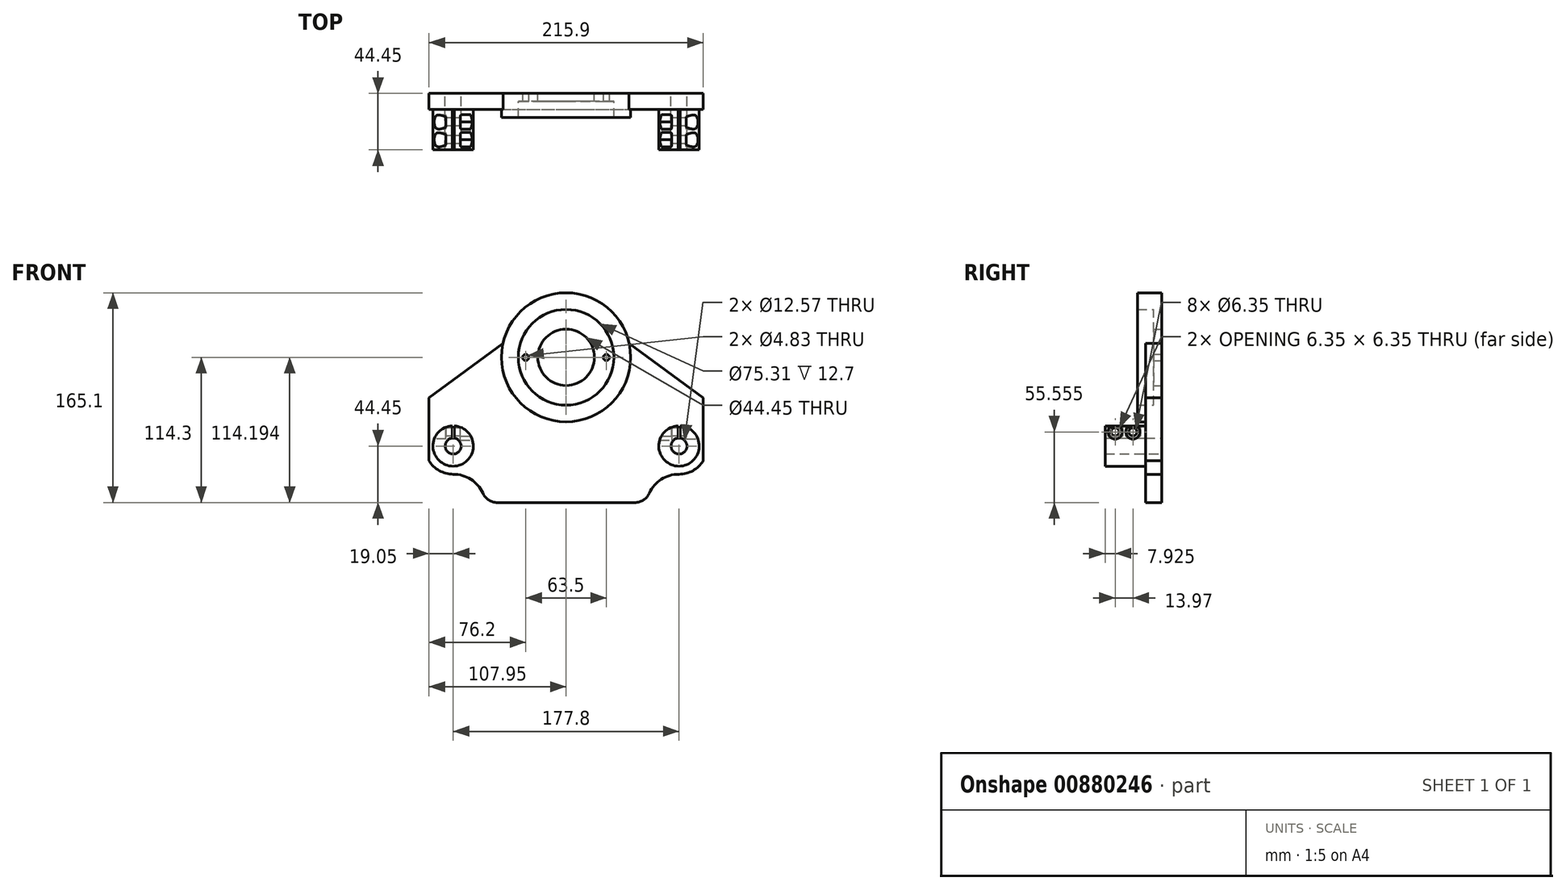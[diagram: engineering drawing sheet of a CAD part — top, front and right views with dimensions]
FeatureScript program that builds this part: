
annotation { "Feature Type Name" : "Feature", "Feature Type Description" : "" }
export const myFeature = defineFeature(function(context is Context, id is Id, definition is map)
    precondition{}
    {
        {
            var Q0;
            Q0=qCreatedBy(makeId("Front.planeOp"),FACE);
            var sketch = newSketch(context, id + "F0", { "sketchPlane" : qUnion([Q0])});
            skCircle(sketch, "E0", {"center": v(-88.9, 0) * mm, "radius": 6.29 * mm});
            skCircle(sketch, "E1", {"center": v(88.9, 0) * mm, "radius": 6.29 * mm});
            skCircle(sketch, "E2", {"center": v(-88.9, -44.45) * mm, "radius": 4.76 * mm});
            skCircle(sketch, "E3", {"center": v(88.9, -44.45) * mm, "radius": 4.76 * mm});
            skLineSegment(sketch, "E4.top", {"start": v(-107.95, -69.85) * mm, "end": v(107.95, -69.85) * mm});
            skLineSegment(sketch, "E4.left", {"start": v(-107.95, 38.1) * mm, "end": v(-107.95, -69.85) * mm});
            skLineSegment(sketch, "E4.right", {"start": v(107.95, 38.1) * mm, "end": v(107.95, -69.85) * mm});
            skPoint(sketch, "E4.middle", {"position": v(0, -15.87) * mm});
            skCircle(sketch, "E5", {"center": v(0, 69.85) * mm, "radius": 37.66 * mm});
            skArc(sketch, "E6", {"start": v(22.5, 100.6) * mm, "mid": v(0, 107.95) * mm, "end": v(-22.5, 100.6) * mm});
            skLineSegment(sketch, "E7", {"start": v(-107.95, 38.1) * mm, "end": v(-22.5, 100.6) * mm});
            skLineSegment(sketch, "E8", {"start": v(107.95, 38.1) * mm, "end": v(22.5, 100.6) * mm});
            skPoint(sketch, "E9.center.orphan", {"position": v(0, 0) * mm});
            skSolve(sketch);
        }
        {
            var Q0;
            Q0=qSketchRegion(id+"F0",true);
            extrude(context, id + "F1", {"entities" : qUnion([Q0]), "depth" : 12.7 * mm});
        }
        {
            var Q0;
            Q0=makeQuery(id+"F1.opExtrude","CAP_FACE",FACE,{"disambiguationData":[OSD([sQuery(id+"F0.wireOp",EDGE,"E9"),sQuery(id+"F0.wireOp",EDGE,"E0"),sQuery(id+"F0.wireOp",EDGE,"E1"),sQuery(id+"F0.wireOp",EDGE,"E2"),sQuery(id+"F0.wireOp",EDGE,"E3"),sQuery(id+"F0.wireOp",EDGE,"E4.bottom"),sQuery(id+"F0.wireOp",EDGE,"E4.top"),sQuery(id+"F0.wireOp",EDGE,"E4.left"),sQuery(id+"F0.wireOp",EDGE,"E4.right")])],"isStart":false});
            var sketch = newSketch(context, id + "F2", { "sketchPlane" : qUnion([Q0])});
            skCircle(sketch, "E10", {"center": v(0, -107.95) * mm, "radius": 63.5 * mm});
            skSolve(sketch);
        }
        {
            var Q0;
            Q0=qSketchRegion(id+"F2",true);
            extrude(context, id + "F3", {"entities" : qUnion([Q0]), "operationType" : NewBodyOperationType.REMOVE, "oppositeDirection" : true, "depth" : 25.4 * mm});
        }
        {
            var Q0;
            Q0=makeQuery(id+"F3.boolean.opBoolean","INTERSECT",EDGE,{"disambiguationData":[OD(0.0)],"derivedFrom":[makeQuery(id+"F1.opExtrude","SWEPT_FACE",FACE,{"disambiguationData":[OSD([sQuery(id+"F0.wireOp",EDGE,"E4.top")])]}),makeQuery(id+"F3.opExtrude","SWEPT_FACE",FACE,{"disambiguationData":[OSD([sQuery(id+"F2.wireOp",EDGE,"E10")])]})]});
            var Q1;
            Q1=makeQuery(id+"F3.boolean.opBoolean","INTERSECT",EDGE,{"disambiguationData":[OD(1.0)],"derivedFrom":[makeQuery(id+"F1.opExtrude","SWEPT_FACE",FACE,{"disambiguationData":[OSD([sQuery(id+"F0.wireOp",EDGE,"E4.top")])]}),makeQuery(id+"F3.opExtrude","SWEPT_FACE",FACE,{"disambiguationData":[OSD([sQuery(id+"F2.wireOp",EDGE,"E10")])]})]});
            fillet(context, id + "F4", {"entities" : qUnion([Q0, Q1]), "radius" : 12.7 * mm, "tangentPropagation" : true, "allowEdgeOverflow" : false});
        }
        {
            var Q0;
            Q0=makeQuery(id+"F1.opExtrude","CAP_FACE",FACE,{"disambiguationData":[OSD([sQuery(id+"F0.wireOp",EDGE,"E9"),sQuery(id+"F0.wireOp",EDGE,"E0"),sQuery(id+"F0.wireOp",EDGE,"E1"),sQuery(id+"F0.wireOp",EDGE,"E2"),sQuery(id+"F0.wireOp",EDGE,"E3"),sQuery(id+"F0.wireOp",EDGE,"E4.bottom"),sQuery(id+"F0.wireOp",EDGE,"E4.top"),sQuery(id+"F0.wireOp",EDGE,"E4.left"),sQuery(id+"F0.wireOp",EDGE,"E4.right")])],"isStart":false});
            var sketch = newSketch(context, id + "F5", { "sketchPlane" : qUnion([Q0])});
            skCircle(sketch, "E11.0", {"center": v(-88.9, 0) * mm, "radius": 6.29 * mm});
            skCircle(sketch, "E12", {"center": v(-88.9, 0) * mm, "radius": 15.88 * mm});
            skCircle(sketch, "E13.0", {"center": v(88.9, 0) * mm, "radius": 6.29 * mm});
            skCircle(sketch, "E14", {"center": v(88.9, 0) * mm, "radius": 15.88 * mm});
            skSolve(sketch);
        }
        {
            var Q0;
            Q0=qSketchRegion(id+"F5",true);
            extrude(context, id + "F6", {"entities" : qUnion([Q0]), "operationType" : NewBodyOperationType.ADD, "depth" : 31.75 * mm});
        }
        {
            var Q0;
            Q0=makeQuery(id+"F6.opExtrude","CAP_FACE",FACE,{"disambiguationData":[OSD([sQuery(id+"F5.wireOp",EDGE,"E11.0"),sQuery(id+"F5.wireOp",EDGE,"E12")])],"isStart":false});
            var sketch = newSketch(context, id + "F7", { "sketchPlane" : qUnion([Q0])});
            skLineSegment(sketch, "E15.bottom", {"start": v(-89.7, 1.72) * mm, "end": v(-88.1, 1.72) * mm});
            skLineSegment(sketch, "E15.top", {"start": v(-89.7, 19.66) * mm, "end": v(-88.1, 19.66) * mm});
            skLineSegment(sketch, "E15.left", {"start": v(-89.7, 1.72) * mm, "end": v(-89.7, 19.66) * mm});
            skLineSegment(sketch, "E15.right", {"start": v(-88.1, 1.72) * mm, "end": v(-88.1, 19.66) * mm});
            skLineSegment(sketch, "E16", {"start": v(-88.9, 1.72) * mm, "end": v(-88.9, 0) * mm});
            skPoint(sketch, "E16.endSnap0", {"position": v(-88.9, 1.72) * mm});
            skLineSegment(sketch, "E17.bottom", {"start": v(88.1, 20.83) * mm, "end": v(89.7, 20.83) * mm});
            skLineSegment(sketch, "E17.top", {"start": v(88.1, 3.08) * mm, "end": v(89.7, 3.08) * mm});
            skLineSegment(sketch, "E17.left", {"start": v(88.1, 20.83) * mm, "end": v(88.1, 3.08) * mm});
            skLineSegment(sketch, "E17.right", {"start": v(89.7, 20.83) * mm, "end": v(89.7, 3.08) * mm});
            skLineSegment(sketch, "E18", {"start": v(88.9, 0) * mm, "end": v(88.9, 3.08) * mm});
            skSolve(sketch);
        }
        {
            var Q0;
            Q0=qSketchRegion(id+"F7",true);
            var Q1;
            Q1=makeQuery(id+"F1.opExtrude","CAP_FACE",FACE,{"disambiguationData":[OSD([sQuery(id+"F0.wireOp",EDGE,"E9"),sQuery(id+"F0.wireOp",EDGE,"E0"),sQuery(id+"F0.wireOp",EDGE,"E1"),sQuery(id+"F0.wireOp",EDGE,"E2"),sQuery(id+"F0.wireOp",EDGE,"E3"),sQuery(id+"F0.wireOp",EDGE,"E4.bottom"),sQuery(id+"F0.wireOp",EDGE,"E4.top"),sQuery(id+"F0.wireOp",EDGE,"E4.left"),sQuery(id+"F0.wireOp",EDGE,"E4.right")])],"isStart":false});
            extrude(context, id + "F8", {"entities" : qUnion([Q0]), "operationType" : NewBodyOperationType.REMOVE, "endBound" : BoundingType.UP_TO_SURFACE, "oppositeDirection" : true, "endBoundEntityFace" : qUnion([Q1]), "depth" : 25.4 * mm});
        }
        {
            var Q0;
            Q0=makeQuery(id+"F1.opExtrude","SWEPT_FACE",FACE,{"disambiguationData":[OSD([sQuery(id+"F0.wireOp",EDGE,"E4.left")])]});
            var sketch = newSketch(context, id + "F9", { "sketchPlane" : qUnion([Q0])});
            skCircle(sketch, "E19", {"center": v(36.53, 11.1) * mm, "radius": 3.18 * mm});
            skCircle(sketch, "E20", {"center": v(22.56, 11.1) * mm, "radius": 3.18 * mm});
            skSolve(sketch);
        }
        {
            var Q0;
            Q0=qSketchRegion(id+"F9",true);
            extrude(context, id + "F10", {"entities" : qUnion([Q0]), "operationType" : NewBodyOperationType.REMOVE, "oppositeDirection" : true, "depth" : 224.54 * mm});
        }
        {
            var Q0;
            Q0=qCreatedBy(makeId("Right.planeOp"),FACE);
            var sketch = newSketch(context, id + "F11", { "sketchPlane" : qUnion([Q0])});
            skCircle(sketch, "E21.0", {"center": v(-36.53, 11.1) * mm, "radius": 3.17 * mm, "construction": true});
            skCircle(sketch, "E22.0", {"center": v(-22.56, 11.1) * mm, "radius": 3.18 * mm, "construction": true});
            skCircle(sketch, "E23.cCircle", {"center": v(-36.53, 11.1) * mm, "radius": 6.6 * mm, "construction": true});
            skLineSegment(sketch, "E23.0", {"start": v(-36.53, 17.7) * mm, "end": v(-30.8, 14.4) * mm});
            skLineSegment(sketch, "E23.1", {"start": v(-30.8, 14.4) * mm, "end": v(-30.8, 7.8) * mm});
            skLineSegment(sketch, "E23.2", {"start": v(-30.8, 7.8) * mm, "end": v(-36.53, 4.5) * mm});
            skLineSegment(sketch, "E23.3", {"start": v(-36.53, 4.5) * mm, "end": v(-42.24, 7.8) * mm});
            skLineSegment(sketch, "E23.4", {"start": v(-42.24, 7.8) * mm, "end": v(-42.24, 14.4) * mm});
            skLineSegment(sketch, "E23.5", {"start": v(-42.24, 14.4) * mm, "end": v(-36.53, 17.7) * mm});
            skCircle(sketch, "E24.cCircle", {"center": v(-22.56, 11.1) * mm, "radius": 6.6 * mm, "construction": true});
            skLineSegment(sketch, "E24.0", {"start": v(-28.27, 14.4) * mm, "end": v(-22.56, 17.7) * mm});
            skLineSegment(sketch, "E24.1", {"start": v(-22.56, 17.7) * mm, "end": v(-16.84, 14.4) * mm});
            skLineSegment(sketch, "E24.2", {"start": v(-16.84, 14.4) * mm, "end": v(-16.84, 7.8) * mm});
            skLineSegment(sketch, "E24.3", {"start": v(-16.84, 7.8) * mm, "end": v(-22.56, 4.5) * mm});
            skLineSegment(sketch, "E24.4", {"start": v(-22.56, 4.5) * mm, "end": v(-28.27, 7.8) * mm});
            skLineSegment(sketch, "E24.5", {"start": v(-28.27, 7.8) * mm, "end": v(-28.27, 14.4) * mm});
            skSolve(sketch);
        }
        {
            var Q0;
            Q0=makeQuery(id+"F11.imprint","IMPRINT",FACE,{"disambiguationData":[TD([[makeQuery(id+"F11.imprint","IMPRINT",EDGE,{"derivedFrom":sQuery(id+"F11.wireOp",EDGE,"E23.0")}),-1.0]])]});
            var Q1;
            Q1=makeQuery(id+"F11.imprint","IMPRINT",FACE,{"disambiguationData":[TD([[makeQuery(id+"F11.imprint","IMPRINT",EDGE,{"derivedFrom":sQuery(id+"F11.wireOp",EDGE,"E24.0")}),-1.0]])]});
            var Q2;
            Q2=sQuery(id+"F11.wireOp",EDGE,"E21.0");
            var Q3;
            Q3=sQuery(id+"F11.wireOp",EDGE,"E22.0");
            extrude(context, id + "F12", {"entities" : qUnion([Q0, Q1]), "operationType" : NewBodyOperationType.REMOVE, "surfaceEntities" : qUnion([Q2, Q3]), "oppositeDirection" : true, "depth" : 83.18 * mm, "hasSecondDirection" : true, "secondDirectionOppositeDirection" : false, "secondDirectionDepth" : 83.18 * mm});
        }
        {
            var Q0;
            Q0=makeQuery(id+"F1.opExtrude","SWEPT_FACE",FACE,{"disambiguationData":[OSD([sQuery(id+"F0.wireOp",EDGE,"E4.left")])]});
            var sketch = newSketch(context, id + "F13", { "sketchPlane" : qUnion([Q0])});
            skCircle(sketch, "E25.0", {"center": v(36.53, 11.1) * mm, "radius": 3.17 * mm, "construction": true});
            skCircle(sketch, "E26.0", {"center": v(22.56, 11.1) * mm, "radius": 3.18 * mm, "construction": true});
            skCircle(sketch, "E27", {"center": v(22.56, 11.1) * mm, "radius": 5.56 * mm});
            skCircle(sketch, "E28", {"center": v(36.53, 11.1) * mm, "radius": 5.56 * mm});
            skSolve(sketch);
        }
        {
            var Q0;
            Q0=qSketchRegion(id+"F13",true);
            extrude(context, id + "F14", {"entities" : qUnion([Q0]), "operationType" : NewBodyOperationType.REMOVE, "oppositeDirection" : true, "depth" : 13.33 * mm});
        }
        {
            var Q0;
            Q0=makeQuery(id+"F1.opExtrude","SWEPT_FACE",FACE,{"disambiguationData":[OSD([sQuery(id+"F0.wireOp",EDGE,"E4.right")])]});
            var sketch = newSketch(context, id + "F15", { "sketchPlane" : qUnion([Q0])});
            skCircle(sketch, "E29.0", {"center": v(-36.53, 11.1) * mm, "radius": 3.17 * mm, "construction": true});
            skCircle(sketch, "E29.1", {"center": v(-22.56, 11.1) * mm, "radius": 3.18 * mm, "construction": true});
            skCircle(sketch, "E30", {"center": v(-36.53, 11.1) * mm, "radius": 5.56 * mm});
            skCircle(sketch, "E31", {"center": v(-22.56, 11.1) * mm, "radius": 5.56 * mm});
            skSolve(sketch);
        }
        {
            var Q0;
            Q0=qSketchRegion(id+"F15",true);
            extrude(context, id + "F16", {"entities" : qUnion([Q0]), "operationType" : NewBodyOperationType.REMOVE, "oppositeDirection" : true, "depth" : 13.33 * mm});
        }
        {
            var Q0;
            {var subQ1=sQuery(id+"F0.wireOp",EDGE,"E4.left");var subQ2=sQuery(id+"F0.wireOp",EDGE,"E4.top");Q0=makeQuery(id+"F3.boolean.opBoolean","SPLIT",FACE,{"disambiguationData":[TD([makeQuery(id+"F1.opExtrude","SWEPT_FACE",FACE,{"disambiguationData":[OSD([subQ1])]})])],"derivedFrom":makeQuery(id+"F1.opExtrude","SWEPT_FACE",FACE,{"disambiguationData":[OSD([subQ2])]})});}
            var sketch = newSketch(context, id + "F17", { "sketchPlane" : qUnion([Q0])});
            skLineSegment(sketch, "E32.0", {"start": v(56.8, 12.7) * mm, "end": v(107.95, 12.7) * mm});
            skLineSegment(sketch, "E33", {"start": v(107.95, 12.7) * mm, "end": v(107.95, 31.75) * mm});
            skLineSegment(sketch, "E34", {"start": v(107.95, 31.75) * mm, "end": v(56.8, 31.75) * mm});
            skLineSegment(sketch, "E35", {"start": v(56.8, 31.75) * mm, "end": v(56.8, 12.7) * mm});
            skCircle(sketch, "E36", {"center": v(82.37, 22.23) * mm, "radius": 3.18 * mm});
            skLineSegment(sketch, "E37", {"start": v(107.95, 22.23) * mm, "end": v(56.8, 22.23) * mm, "construction": true});
            skLineSegment(sketch, "E38.bottom", {"start": v(-107.95, 12.7) * mm, "end": v(-56.8, 12.7) * mm});
            skLineSegment(sketch, "E38.top", {"start": v(-107.95, 31.75) * mm, "end": v(-56.8, 31.75) * mm});
            skLineSegment(sketch, "E38.left", {"start": v(-107.95, 12.7) * mm, "end": v(-107.95, 31.75) * mm});
            skLineSegment(sketch, "E38.right", {"start": v(-56.8, 12.7) * mm, "end": v(-56.8, 31.75) * mm});
            skCircle(sketch, "E39", {"center": v(-82.37, 22.22) * mm, "radius": 3.18 * mm});
            skPoint(sketch, "E39.centerSnap0", {"position": v(-82.37, 31.75) * mm});
            skSolve(sketch);
        }
        {
            var Q0;
            Q0=qSketchRegion(id+"F17",true);
            extrude(context, id + "F18", {"entities" : qUnion([Q0]), "operationType" : NewBodyOperationType.ADD, "oppositeDirection" : true, "depth" : 4.75 * mm});
        }
        {
            var Q0;
            Q0=makeQuery(id+"F18.opExtrude","SWEPT_EDGE",EDGE,{"disambiguationData":[OSD([sQuery(id+"F17.wireOp",EDGE,"E34"),sQuery(id+"F17.wireOp",EDGE,"E35")])]});
            var Q1;
            Q1=makeQuery(id+"F18.opExtrude","SWEPT_EDGE",EDGE,{"disambiguationData":[OSD([sQuery(id+"F17.wireOp",EDGE,"E33"),sQuery(id+"F17.wireOp",EDGE,"E34")])]});
            var Q2;
            Q2=makeQuery(id+"F18.opExtrude","SWEPT_EDGE",EDGE,{"disambiguationData":[OSD([sQuery(id+"F17.wireOp",EDGE,"E38.top"),sQuery(id+"F17.wireOp",EDGE,"E38.right")])]});
            var Q3;
            Q3=makeQuery(id+"F18.opExtrude","SWEPT_EDGE",EDGE,{"disambiguationData":[OSD([sQuery(id+"F17.wireOp",EDGE,"E38.top"),sQuery(id+"F17.wireOp",EDGE,"E38.left")])]});
            fillet(context, id + "F19", {"entities" : qUnion([Q0, Q1, Q2, Q3]), "radius" : 12.7 * mm, "tangentPropagation" : true, "allowEdgeOverflow" : false});
        }
        {
            var Q0;
            {var subQ0=sQuery(id+"F0.wireOp",EDGE,"E8");var subQ1=sQuery(id+"F0.wireOp",EDGE,"E7");var subQ2=sQuery(id+"F0.wireOp",EDGE,"E6");var subQ3=sQuery(id+"F0.wireOp",EDGE,"E5");var subQ4=sQuery(id+"F0.wireOp",EDGE,"E4.right");var subQ5=sQuery(id+"F0.wireOp",EDGE,"E4.left");var subQ6=sQuery(id+"F0.wireOp",EDGE,"E4.top");var subQ7=sQuery(id+"F0.wireOp",EDGE,"E3");var subQ8=sQuery(id+"F0.wireOp",EDGE,"E2");var subQ9=sQuery(id+"F0.wireOp",EDGE,"E1");var subQ10=sQuery(id+"F0.wireOp",EDGE,"E0");var subQ11=sQuery(id+"F7.wireOp",EDGE,"E15.bottom");Q0=makeQuery(id+"F8.boolean.opBoolean","MERGE",FACE,{"derivedFrom":[makeQuery(id+"F1.opExtrude","CAP_FACE",FACE,{"disambiguationData":[OSD([subQ10,subQ9,subQ8,subQ7,subQ6,subQ5,subQ4,subQ3,subQ2,subQ1,subQ0])],"isStart":false}),makeQuery(id+"F8.opExtrude","CAP_FACE",FACE,{"disambiguationData":[OSD([subQ10,subQ9,subQ8,subQ7,subQ6,subQ5,subQ4,subQ3,subQ2,subQ1,subQ0]),ownerDisambiguation([makeQuery(id+"F7.imprint","IMPRINT",EDGE,{"disambiguationData":[TD([[makeQuery(id+"F7.imprint","IMPRINT",VERTEX,{"derivedFrom":subQ11}),1.0]])],"derivedFrom":subQ11})])],"isStart":false}),makeQuery(id+"F8.opExtrude","CAP_FACE",FACE,{"disambiguationData":[OSD([subQ10,subQ9,subQ8,subQ7,subQ6,subQ5,subQ4,subQ3,subQ2,subQ1,subQ0]),ownerDisambiguation([makeQuery(id+"F7.imprint","IMPRINT",EDGE,{"derivedFrom":sQuery(id+"F7.wireOp",EDGE,"E17.bottom")})])],"isStart":false})]});}
            var sketch = newSketch(context, id + "F20", { "sketchPlane" : qUnion([Q0])});
            skCircle(sketch, "E40", {"center": v(0, 69.85) * mm, "radius": 50.8 * mm});
            skCircle(sketch, "E41.0", {"center": v(0, 69.85) * mm, "radius": 37.66 * mm});
            skSolve(sketch);
        }
        {
            var Q0;
            Q0=qSketchRegion(id+"F20",true);
            extrude(context, id + "F21", {"entities" : qUnion([Q0]), "operationType" : NewBodyOperationType.ADD, "oppositeDirection" : true, "depth" : 12.7 * mm});
        }
        {
            var Q0;
            Q0=makeQuery(id+"F21.boolean.opBoolean","MERGE",FACE,{"derivedFrom":[makeQuery(id+"F1.opExtrude","CAP_FACE",FACE,{"disambiguationData":[OSD([sQuery(id+"F0.wireOp",EDGE,"E0"),sQuery(id+"F0.wireOp",EDGE,"E1"),sQuery(id+"F0.wireOp",EDGE,"E2"),sQuery(id+"F0.wireOp",EDGE,"E3"),sQuery(id+"F0.wireOp",EDGE,"E4.top"),sQuery(id+"F0.wireOp",EDGE,"E4.left"),sQuery(id+"F0.wireOp",EDGE,"E4.right"),sQuery(id+"F0.wireOp",EDGE,"E5"),sQuery(id+"F0.wireOp",EDGE,"E6"),sQuery(id+"F0.wireOp",EDGE,"E7"),sQuery(id+"F0.wireOp",EDGE,"E8")])],"isStart":true}),makeQuery(id+"F21.opExtrude","CAP_FACE",FACE,{"disambiguationData":[OSD([sQuery(id+"F20.wireOp",EDGE,"E40"),sQuery(id+"F20.wireOp",EDGE,"E41.0")])],"isStart":false})]});
            var sketch = newSketch(context, id + "F22", { "sketchPlane" : qUnion([Q0])});
            skCircle(sketch, "E42.0", {"center": v(0, 69.85) * mm, "radius": 37.66 * mm});
            skCircle(sketch, "E43", {"center": v(0, 69.85) * mm, "radius": 22.23 * mm});
            skSolve(sketch);
        }
        {
            var Q0;
            Q0=qSketchRegion(id+"F22",true);
            extrude(context, id + "F23", {"entities" : qUnion([Q0]), "operationType" : NewBodyOperationType.ADD, "oppositeDirection" : true, "depth" : 6.35 * mm});
        }
        {
            var Q0;
            Q0=makeQuery(id+"F23.boolean.opBoolean","MERGE",FACE,{"derivedFrom":[makeQuery(id+"F21.boolean.opBoolean","MERGE",FACE,{"derivedFrom":[makeQuery(id+"F1.opExtrude","CAP_FACE",FACE,{"disambiguationData":[OSD([sQuery(id+"F0.wireOp",EDGE,"E0"),sQuery(id+"F0.wireOp",EDGE,"E1"),sQuery(id+"F0.wireOp",EDGE,"E2"),sQuery(id+"F0.wireOp",EDGE,"E3"),sQuery(id+"F0.wireOp",EDGE,"E4.top"),sQuery(id+"F0.wireOp",EDGE,"E4.left"),sQuery(id+"F0.wireOp",EDGE,"E4.right"),sQuery(id+"F0.wireOp",EDGE,"E5"),sQuery(id+"F0.wireOp",EDGE,"E6"),sQuery(id+"F0.wireOp",EDGE,"E7"),sQuery(id+"F0.wireOp",EDGE,"E8")])],"isStart":true}),makeQuery(id+"F21.opExtrude","CAP_FACE",FACE,{"disambiguationData":[OSD([sQuery(id+"F20.wireOp",EDGE,"E40"),sQuery(id+"F20.wireOp",EDGE,"E41.0")])],"isStart":false})]}),makeQuery(id+"F23.opExtrude","CAP_FACE",FACE,{"disambiguationData":[OSD([sQuery(id+"F22.wireOp",EDGE,"E42.0"),sQuery(id+"F22.wireOp",EDGE,"E43")])],"isStart":true})]});
            var sketch = newSketch(context, id + "F24", { "sketchPlane" : qUnion([Q0])});
            skCircle(sketch, "E44", {"center": v(-31.75, 69.74) * mm, "radius": 2.41 * mm});
            skCircle(sketch, "E45", {"center": v(31.75, 69.74) * mm, "radius": 2.41 * mm});
            skLineSegment(sketch, "E46", {"start": v(-31.75, 69.74) * mm, "end": v(0, 69.74) * mm, "construction": true});
            skLineSegment(sketch, "E47", {"start": v(0, 69.74) * mm, "end": v(31.75, 69.74) * mm, "construction": true});
            skSolve(sketch);
        }
        {
            var Q0;
            Q0=qSketchRegion(id+"F24",true);
            extrude(context, id + "F25", {"entities" : qUnion([Q0]), "operationType" : NewBodyOperationType.REMOVE, "oppositeDirection" : true, "depth" : 25.4 * mm});
        }
        {
            var Q0;
            {var subQ0=sQuery(id+"F0.wireOp",EDGE,"E8");var subQ1=sQuery(id+"F0.wireOp",EDGE,"E7");var subQ2=sQuery(id+"F0.wireOp",EDGE,"E6");var subQ3=sQuery(id+"F0.wireOp",EDGE,"E5");var subQ4=sQuery(id+"F0.wireOp",EDGE,"E4.right");var subQ5=sQuery(id+"F0.wireOp",EDGE,"E4.left");var subQ6=sQuery(id+"F0.wireOp",EDGE,"E4.top");var subQ7=sQuery(id+"F0.wireOp",EDGE,"E3");var subQ8=sQuery(id+"F0.wireOp",EDGE,"E2");var subQ9=sQuery(id+"F0.wireOp",EDGE,"E1");var subQ10=sQuery(id+"F0.wireOp",EDGE,"E0");var subQ11=sQuery(id+"F7.wireOp",EDGE,"E15.bottom");Q0=makeQuery(id+"F21.boolean.opBoolean","MERGE",FACE,{"derivedFrom":[makeQuery(id+"F8.boolean.opBoolean","MERGE",FACE,{"derivedFrom":[makeQuery(id+"F1.opExtrude","CAP_FACE",FACE,{"disambiguationData":[OSD([subQ10,subQ9,subQ8,subQ7,subQ6,subQ5,subQ4,subQ3,subQ2,subQ1,subQ0])],"isStart":false}),makeQuery(id+"F8.opExtrude","CAP_FACE",FACE,{"disambiguationData":[OSD([subQ10,subQ9,subQ8,subQ7,subQ6,subQ5,subQ4,subQ3,subQ2,subQ1,subQ0]),ownerDisambiguation([makeQuery(id+"F7.imprint","IMPRINT",EDGE,{"disambiguationData":[TD([[makeQuery(id+"F7.imprint","IMPRINT",VERTEX,{"derivedFrom":subQ11}),1.0]])],"derivedFrom":subQ11})])],"isStart":false}),makeQuery(id+"F8.opExtrude","CAP_FACE",FACE,{"disambiguationData":[OSD([subQ10,subQ9,subQ8,subQ7,subQ6,subQ5,subQ4,subQ3,subQ2,subQ1,subQ0]),ownerDisambiguation([makeQuery(id+"F7.imprint","IMPRINT",EDGE,{"derivedFrom":sQuery(id+"F7.wireOp",EDGE,"E17.bottom")})])],"isStart":false})]}),makeQuery(id+"F21.opExtrude","CAP_FACE",FACE,{"disambiguationData":[OSD([sQuery(id+"F20.wireOp",EDGE,"E40"),sQuery(id+"F20.wireOp",EDGE,"E41.0")])],"isStart":true})]});}
            var sketch = newSketch(context, id + "F26", { "sketchPlane" : qUnion([Q0])});
            skCircle(sketch, "E48.0", {"center": v(0, 69.85) * mm, "radius": 37.66 * mm});
            skCircle(sketch, "E49", {"center": v(0, 69.85) * mm, "radius": 50.8 * mm});
            skSolve(sketch);
        }
        {
            var Q0;
            Q0=qSketchRegion(id+"F26",true);
            extrude(context, id + "F27", {"entities" : qUnion([Q0]), "operationType" : NewBodyOperationType.ADD, "depth" : 6.35 * mm});
        }
        {
            var Q0;
            {var subQ0=sQuery(id+"F0.wireOp",EDGE,"E8");var subQ1=sQuery(id+"F0.wireOp",EDGE,"E7");var subQ2=sQuery(id+"F0.wireOp",EDGE,"E6");var subQ3=sQuery(id+"F0.wireOp",EDGE,"E5");var subQ4=sQuery(id+"F0.wireOp",EDGE,"E4.right");var subQ5=sQuery(id+"F0.wireOp",EDGE,"E4.left");var subQ6=sQuery(id+"F0.wireOp",EDGE,"E4.top");var subQ7=sQuery(id+"F0.wireOp",EDGE,"E3");var subQ8=sQuery(id+"F0.wireOp",EDGE,"E2");var subQ9=sQuery(id+"F0.wireOp",EDGE,"E1");var subQ10=sQuery(id+"F0.wireOp",EDGE,"E0");var subQ11=sQuery(id+"F7.wireOp",EDGE,"E15.bottom");Q0=makeQuery(id+"F21.boolean.opBoolean","MERGE",FACE,{"derivedFrom":[makeQuery(id+"F8.boolean.opBoolean","MERGE",FACE,{"derivedFrom":[makeQuery(id+"F1.opExtrude","CAP_FACE",FACE,{"disambiguationData":[OSD([subQ10,subQ9,subQ8,subQ7,subQ6,subQ5,subQ4,subQ3,subQ2,subQ1,subQ0])],"isStart":false}),makeQuery(id+"F8.opExtrude","CAP_FACE",FACE,{"disambiguationData":[OSD([subQ10,subQ9,subQ8,subQ7,subQ6,subQ5,subQ4,subQ3,subQ2,subQ1,subQ0]),ownerDisambiguation([makeQuery(id+"F7.imprint","IMPRINT",EDGE,{"disambiguationData":[TD([[makeQuery(id+"F7.imprint","IMPRINT",VERTEX,{"derivedFrom":subQ11}),1.0]])],"derivedFrom":subQ11})])],"isStart":false}),makeQuery(id+"F8.opExtrude","CAP_FACE",FACE,{"disambiguationData":[OSD([subQ10,subQ9,subQ8,subQ7,subQ6,subQ5,subQ4,subQ3,subQ2,subQ1,subQ0]),ownerDisambiguation([makeQuery(id+"F7.imprint","IMPRINT",EDGE,{"derivedFrom":sQuery(id+"F7.wireOp",EDGE,"E17.bottom")})])],"isStart":false})]}),makeQuery(id+"F21.opExtrude","CAP_FACE",FACE,{"disambiguationData":[OSD([sQuery(id+"F20.wireOp",EDGE,"E40"),sQuery(id+"F20.wireOp",EDGE,"E41.0")])],"isStart":true})]});}
            var sketch = newSketch(context, id + "F28", { "sketchPlane" : qUnion([Q0])});
            skArc(sketch, "E50", {"start": v(-111.1, 1.11) * mm, "mid": v(-92.44, -21.94) * mm, "end": v(-67.48, -5.93) * mm});
            skArc(sketch, "E51", {"start": v(67.48, -5.93) * mm, "mid": v(92.52, -21.93) * mm, "end": v(111.09, 1.27) * mm});
            skLineSegment(sketch, "E52", {"start": v(-43, 12.7) * mm, "end": v(43, 12.7) * mm});
            skLineSegment(sketch, "E53", {"start": v(-111.1, 1.11) * mm, "end": v(-111.1, -81.42) * mm});
            skLineSegment(sketch, "E54", {"start": v(-111.1, -81.42) * mm, "end": v(111.09, -81.42) * mm});
            skLineSegment(sketch, "E55", {"start": v(111.09, -81.42) * mm, "end": v(111.09, 1.27) * mm});
            skLineSegment(sketch, "E56", {"start": v(0, 12.7) * mm, "end": v(0, 0) * mm, "construction": true});
            skPoint(sketch, "E57.newPointB", {"position": v(38.1, 12.7) * mm});
            skArc(sketch, "E57.filletArc", {"start": v(67.48, -5.93) * mm, "mid": v(58.38, 7.51) * mm, "end": v(43, 12.7) * mm});
            skPoint(sketch, "E58.newPointB", {"position": v(-38.1, 12.7) * mm});
            skArc(sketch, "E58.filletArc", {"start": v(-43, 12.7) * mm, "mid": v(-58.38, 7.51) * mm, "end": v(-67.48, -5.93) * mm});
            skSolve(sketch);
        }
        {
            var Q0;
            Q0=qSketchRegion(id+"F28",true);
            extrude(context, id + "F29", {"entities" : qUnion([Q0]), "operationType" : NewBodyOperationType.REMOVE, "oppositeDirection" : true, "depth" : 25.4 * mm, "hasSecondDirection" : true, "secondDirectionOppositeDirection" : false, "secondDirectionDepth" : 25.4 * mm});
        }
        {
            var Q0;
            {var subQ0=sQuery(id+"F0.wireOp",EDGE,"E8");var subQ1=sQuery(id+"F0.wireOp",EDGE,"E7");var subQ2=sQuery(id+"F0.wireOp",EDGE,"E6");var subQ3=sQuery(id+"F0.wireOp",EDGE,"E5");var subQ4=sQuery(id+"F0.wireOp",EDGE,"E4.right");var subQ5=sQuery(id+"F0.wireOp",EDGE,"E4.left");var subQ6=sQuery(id+"F0.wireOp",EDGE,"E4.top");var subQ7=sQuery(id+"F0.wireOp",EDGE,"E3");var subQ8=sQuery(id+"F0.wireOp",EDGE,"E2");var subQ9=sQuery(id+"F0.wireOp",EDGE,"E1");var subQ10=sQuery(id+"F0.wireOp",EDGE,"E0");var subQ11=sQuery(id+"F7.wireOp",EDGE,"E15.bottom");Q0=makeQuery(id+"F21.boolean.opBoolean","MERGE",FACE,{"derivedFrom":[makeQuery(id+"F8.boolean.opBoolean","MERGE",FACE,{"derivedFrom":[makeQuery(id+"F1.opExtrude","CAP_FACE",FACE,{"disambiguationData":[OSD([subQ10,subQ9,subQ8,subQ7,subQ6,subQ5,subQ4,subQ3,subQ2,subQ1,subQ0])],"isStart":false}),makeQuery(id+"F8.opExtrude","CAP_FACE",FACE,{"disambiguationData":[OSD([subQ10,subQ9,subQ8,subQ7,subQ6,subQ5,subQ4,subQ3,subQ2,subQ1,subQ0]),ownerDisambiguation([makeQuery(id+"F7.imprint","IMPRINT",EDGE,{"disambiguationData":[TD([[makeQuery(id+"F7.imprint","IMPRINT",VERTEX,{"derivedFrom":subQ11}),1.0]])],"derivedFrom":subQ11})])],"isStart":false}),makeQuery(id+"F8.opExtrude","CAP_FACE",FACE,{"disambiguationData":[OSD([subQ10,subQ9,subQ8,subQ7,subQ6,subQ5,subQ4,subQ3,subQ2,subQ1,subQ0]),ownerDisambiguation([makeQuery(id+"F7.imprint","IMPRINT",EDGE,{"derivedFrom":sQuery(id+"F7.wireOp",EDGE,"E17.bottom")})])],"isStart":false})]}),makeQuery(id+"F21.opExtrude","CAP_FACE",FACE,{"disambiguationData":[OSD([sQuery(id+"F20.wireOp",EDGE,"E40"),sQuery(id+"F20.wireOp",EDGE,"E41.0")])],"isStart":true})]});}
            var sketch = newSketch(context, id + "F30", { "sketchPlane" : qUnion([Q0])});
            skLineSegment(sketch, "E59.bottom", {"start": v(-60.33, 16.45) * mm, "end": v(60.33, 16.45) * mm});
            skLineSegment(sketch, "E59.top", {"start": v(-88.9, -22.23) * mm, "end": v(88.9, -22.23) * mm});
            skPoint(sketch, "E59.middle", {"position": v(0, -11.72) * mm});
            skLineSegment(sketch, "E60", {"start": v(0, -22.23) * mm, "end": v(0, 16.45) * mm, "construction": true});
            skLineSegment(sketch, "E61", {"start": v(-88.9, -22.22) * mm, "end": v(-72.75, -10.3) * mm});
            skLineSegment(sketch, "E62", {"start": v(-72.75, -10.3) * mm, "end": v(-60.32, 16.45) * mm});
            skLineSegment(sketch, "E63", {"start": v(88.9, -22.22) * mm, "end": v(72.75, -10.3) * mm});
            skLineSegment(sketch, "E64", {"start": v(72.75, -10.3) * mm, "end": v(60.33, 16.45) * mm});
            skSolve(sketch);
        }
        {
            var Q0;
            Q0=qSketchRegion(id+"F30",true);
            extrude(context, id + "F31", {"entities" : qUnion([Q0]), "operationType" : NewBodyOperationType.ADD, "oppositeDirection" : true, "depth" : 12.7 * mm});
        }
        {
            var Q0;
            {var subQ0=sQuery(id+"F0.wireOp",EDGE,"E8");var subQ1=sQuery(id+"F0.wireOp",EDGE,"E7");var subQ2=sQuery(id+"F0.wireOp",EDGE,"E6");var subQ3=sQuery(id+"F0.wireOp",EDGE,"E5");var subQ4=sQuery(id+"F0.wireOp",EDGE,"E4.right");var subQ5=sQuery(id+"F0.wireOp",EDGE,"E4.left");var subQ6=sQuery(id+"F0.wireOp",EDGE,"E4.top");var subQ7=sQuery(id+"F0.wireOp",EDGE,"E3");var subQ8=sQuery(id+"F0.wireOp",EDGE,"E2");var subQ9=sQuery(id+"F0.wireOp",EDGE,"E1");var subQ10=sQuery(id+"F0.wireOp",EDGE,"E0");var subQ11=sQuery(id+"F7.wireOp",EDGE,"E15.bottom");Q0=makeQuery(id+"F31.boolean.opBoolean","MERGE",FACE,{"derivedFrom":[makeQuery(id+"F21.boolean.opBoolean","MERGE",FACE,{"derivedFrom":[makeQuery(id+"F8.boolean.opBoolean","MERGE",FACE,{"derivedFrom":[makeQuery(id+"F1.opExtrude","CAP_FACE",FACE,{"disambiguationData":[OSD([subQ10,subQ9,subQ8,subQ7,subQ6,subQ5,subQ4,subQ3,subQ2,subQ1,subQ0])],"isStart":false}),makeQuery(id+"F8.opExtrude","CAP_FACE",FACE,{"disambiguationData":[OSD([subQ10,subQ9,subQ8,subQ7,subQ6,subQ5,subQ4,subQ3,subQ2,subQ1,subQ0]),ownerDisambiguation([makeQuery(id+"F7.imprint","IMPRINT",EDGE,{"disambiguationData":[TD([[makeQuery(id+"F7.imprint","IMPRINT",VERTEX,{"derivedFrom":subQ11}),1.0]])],"derivedFrom":subQ11})])],"isStart":false}),makeQuery(id+"F8.opExtrude","CAP_FACE",FACE,{"disambiguationData":[OSD([subQ10,subQ9,subQ8,subQ7,subQ6,subQ5,subQ4,subQ3,subQ2,subQ1,subQ0]),ownerDisambiguation([makeQuery(id+"F7.imprint","IMPRINT",EDGE,{"derivedFrom":sQuery(id+"F7.wireOp",EDGE,"E17.bottom")})])],"isStart":false})]}),makeQuery(id+"F21.opExtrude","CAP_FACE",FACE,{"disambiguationData":[OSD([sQuery(id+"F20.wireOp",EDGE,"E40"),sQuery(id+"F20.wireOp",EDGE,"E41.0")])],"isStart":true})]}),makeQuery(id+"F31.opExtrude","CAP_FACE",FACE,{"disambiguationData":[OSD([sQuery(id+"F30.wireOp",EDGE,"E59.bottom"),sQuery(id+"F30.wireOp",EDGE,"E59.top"),sQuery(id+"F30.wireOp",EDGE,"E61"),sQuery(id+"F30.wireOp",EDGE,"E62"),sQuery(id+"F30.wireOp",EDGE,"E63"),sQuery(id+"F30.wireOp",EDGE,"E64")])],"isStart":true})]});}
            var sketch = newSketch(context, id + "F32", { "sketchPlane" : qUnion([Q0])});
            skLineSegment(sketch, "E65.bottom", {"start": v(-63.5, -44.45) * mm, "end": v(63.5, -44.45) * mm});
            skLineSegment(sketch, "E65.top", {"start": v(-63.5, 19.05) * mm, "end": v(63.5, 19.05) * mm});
            skLineSegment(sketch, "E65.left", {"start": v(-63.5, -44.45) * mm, "end": v(-63.5, 19.05) * mm});
            skLineSegment(sketch, "E65.right", {"start": v(63.5, -44.45) * mm, "end": v(63.5, 19.05) * mm});
            skPoint(sketch, "E65.middle", {"position": v(0, -12.7) * mm});
            skSolve(sketch);
        }
        {
            var Q0;
            Q0=qSketchRegion(id+"F32",true);
            extrude(context, id + "F33", {"entities" : qUnion([Q0]), "operationType" : NewBodyOperationType.ADD, "oppositeDirection" : true, "depth" : 12.7 * mm});
        }
        {
            var Q0;
            Q0=makeQuery(id+"F33.boolean.opBoolean","INTERSECT",EDGE,{"derivedFrom":[makeQuery(id+"F31.opExtrude","SWEPT_FACE",FACE,{"disambiguationData":[OSD([sQuery(id+"F30.wireOp",EDGE,"E59.top")])]}),makeQuery(id+"F33.opExtrude","SWEPT_FACE",FACE,{"disambiguationData":[OSD([sQuery(id+"F32.wireOp",EDGE,"E65.left")])]})]});
            var Q1;
            Q1=makeQuery(id+"F33.boolean.opBoolean","INTERSECT",EDGE,{"derivedFrom":[makeQuery(id+"F31.opExtrude","SWEPT_FACE",FACE,{"disambiguationData":[OSD([sQuery(id+"F30.wireOp",EDGE,"E59.top")])]}),makeQuery(id+"F33.opExtrude","SWEPT_FACE",FACE,{"disambiguationData":[OSD([sQuery(id+"F32.wireOp",EDGE,"E65.right")])]})]});
            fillet(context, id + "F34", {"entities" : qUnion([Q0, Q1]), "radius" : 25.4 * mm, "tangentPropagation" : true, "allowEdgeOverflow" : false});
        }
        {
            var Q0;
            Q0=makeQuery(id+"F34.opFillet","BLEND_EDGE",EDGE,{"blendedFrom":[makeQuery(id+"F33.boolean.opBoolean","INTERSECT",EDGE,{"derivedFrom":[makeQuery(id+"F31.opExtrude","SWEPT_FACE",FACE,{"disambiguationData":[OSD([sQuery(id+"F30.wireOp",EDGE,"E59.top")])]}),makeQuery(id+"F33.opExtrude","SWEPT_FACE",FACE,{"disambiguationData":[OSD([sQuery(id+"F32.wireOp",EDGE,"E65.left")])]})]}),makeQuery(id+"F33.opExtrude","SWEPT_FACE",FACE,{"disambiguationData":[OSD([sQuery(id+"F32.wireOp",EDGE,"E65.bottom")])]})],"blendedInto":[makeQuery(id+"F33.opExtrude","SWEPT_FACE",FACE,{"disambiguationData":[OSD([sQuery(id+"F32.wireOp",EDGE,"E65.bottom")])]})]});
            var Q1;
            Q1=makeQuery(id+"F34.opFillet","BLEND_EDGE",EDGE,{"blendedFrom":[makeQuery(id+"F33.boolean.opBoolean","INTERSECT",EDGE,{"derivedFrom":[makeQuery(id+"F31.opExtrude","SWEPT_FACE",FACE,{"disambiguationData":[OSD([sQuery(id+"F30.wireOp",EDGE,"E59.top")])]}),makeQuery(id+"F33.opExtrude","SWEPT_FACE",FACE,{"disambiguationData":[OSD([sQuery(id+"F32.wireOp",EDGE,"E65.right")])]})]}),makeQuery(id+"F33.opExtrude","SWEPT_FACE",FACE,{"disambiguationData":[OSD([sQuery(id+"F32.wireOp",EDGE,"E65.bottom")])]})],"blendedInto":[makeQuery(id+"F33.opExtrude","SWEPT_FACE",FACE,{"disambiguationData":[OSD([sQuery(id+"F32.wireOp",EDGE,"E65.bottom")])]})]});
            fillet(context, id + "F35", {"entities" : qUnion([Q0, Q1]), "radius" : 12.7 * mm, "tangentPropagation" : true, "allowEdgeOverflow" : false});
        }
    });
